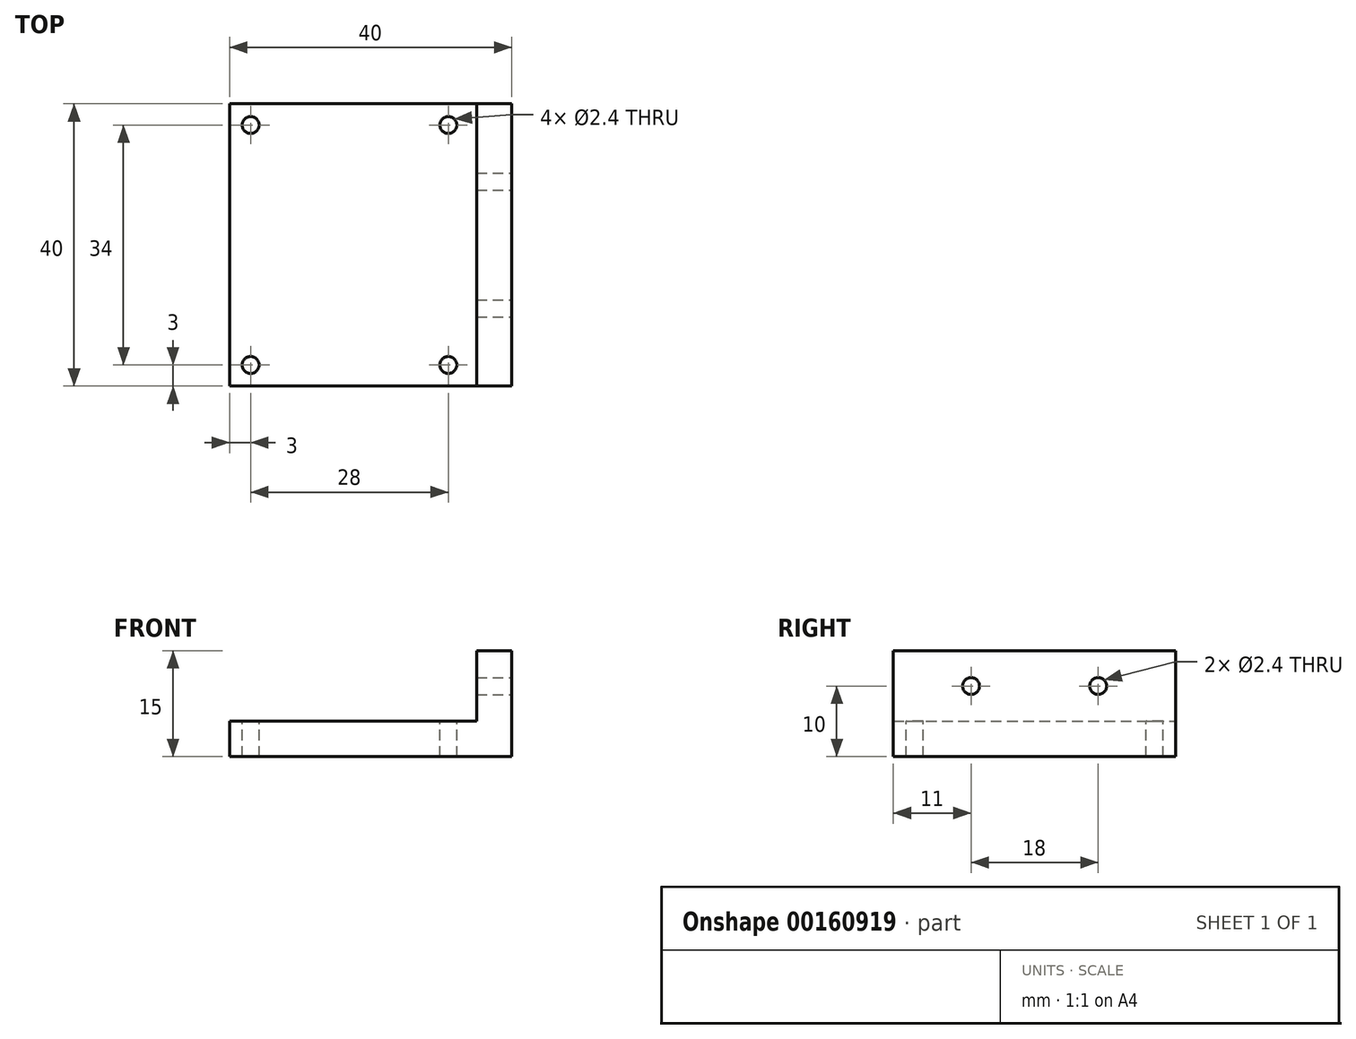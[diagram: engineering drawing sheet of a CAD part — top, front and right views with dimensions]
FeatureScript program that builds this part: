
annotation { "Feature Type Name" : "Feature", "Feature Type Description" : "" }
export const myFeature = defineFeature(function(context is Context, id is Id, definition is map)
    precondition{}
    {
        {
            var Q0;
            Q0=qCreatedBy(makeId("Top.planeOp"),FACE);
            var sketch = newSketch(context, id + "F0", { "sketchPlane" : qUnion([Q0])});
            skLineSegment(sketch, "E0.bottom", {"start": v(20, -20) * mm, "end": v(-20, -20) * mm});
            skLineSegment(sketch, "E0.top", {"start": v(20, 20) * mm, "end": v(-20, 20) * mm});
            skLineSegment(sketch, "E0.left", {"start": v(20, -20) * mm, "end": v(20, 20) * mm});
            skLineSegment(sketch, "E0.right", {"start": v(-20, -20) * mm, "end": v(-20, 20) * mm});
            skPoint(sketch, "E0.middle", {"position": v(0, 0) * mm});
            skSolve(sketch);
        }
        {
            var Q0;
            Q0 = qSketchRegion(id + "F0", true);
            extrude(context, id + "F1", {"entities" : qUnion([Q0]), "depth" : 5 * mm});
        }
        {
            var Q0;
            Q0=makeQuery(id+"F1.opExtrude","CAP_FACE",FACE,{"disambiguationData":[OSD([sQuery(id+"F0.wireOp",EDGE,"E0.bottom"),sQuery(id+"F0.wireOp",EDGE,"E0.top"),sQuery(id+"F0.wireOp",EDGE,"E0.left"),sQuery(id+"F0.wireOp",EDGE,"E0.right")])],"isStart":false});
            var sketch = newSketch(context, id + "F2", { "sketchPlane" : qUnion([Q0])});
            skLineSegment(sketch, "E1.bottom", {"start": v(20, 20) * mm, "end": v(15, 20) * mm});
            skLineSegment(sketch, "E1.top", {"start": v(20, -20) * mm, "end": v(15, -20) * mm});
            skLineSegment(sketch, "E1.left", {"start": v(20, 20) * mm, "end": v(20, -20) * mm});
            skLineSegment(sketch, "E1.right", {"start": v(15, 20) * mm, "end": v(15, -20) * mm});
            skSolve(sketch);
        }
        {
            var Q0;
            Q0 = qSketchRegion(id + "F2", true);
            extrude(context, id + "F3", {"entities" : qUnion([Q0]), "operationType" : NewBodyOperationType.ADD, "depth" : 10 * mm});
        }
        {
            var Q0;
            Q0=makeQuery(id+"F3.boolean.opBoolean","MERGE",FACE,{"derivedFrom":[makeQuery(id+"F1.opExtrude","SWEPT_FACE",FACE,{"disambiguationData":[OSD([sQuery(id+"F0.wireOp",EDGE,"E0.left")])]}),makeQuery(id+"F3.opExtrude","SWEPT_FACE",FACE,{"disambiguationData":[OSD([sQuery(id+"F2.wireOp",EDGE,"E1.left")])]})]});
            var sketch = newSketch(context, id + "F4", { "sketchPlane" : qUnion([Q0])});
            skPoint(sketch, "E2", {"position": v(-9, 10) * mm});
            skPoint(sketch, "E3", {"position": v(9, 10) * mm});
            skSolve(sketch);
        }
        {
            var Q0;
            Q0=sQuery(id+"F4.wireOp",VERTEX,"E2");
            var Q1;
            Q1=sQuery(id+"F4.wireOp",VERTEX,"E3");
            var Q2;
            Q2=makeQuery(id+"F1.opExtrude","SWEPT_BODY",BODY,{"disambiguationData":[OSD([sQuery(id+"F0.wireOp",EDGE,"E0.bottom"),sQuery(id+"F0.wireOp",EDGE,"E0.top"),sQuery(id+"F0.wireOp",EDGE,"E0.left"),sQuery(id+"F0.wireOp",EDGE,"E0.right")])]});
            hole(context, id + "F5", {"style" : HoleStyle.SIMPLE, "endStyle" : HoleEndStyle.THROUGH, "standardTappedOrClearance" : lookupTablePath({ "standard" : "ISO", "engagement" : "75%", "pitch" : "0.6 mm", "size" : "M3", "type" : "Tapped" }), "standardBlindInLast" : lookupTablePath({ "standard" : "ISO", "engagement" : "75%", "pitch" : "0.6 mm", "size" : "M3", "type" : "Tapped" }), "holeDiameter" : 2.4 * mm, "locations" : qUnion([Q0, Q1]), "scope" : qUnion([Q2]), "isTappedThrough" : true, "showTappedDepth" : true});
        }
        {
            var Q0;
            Q0=makeQuery(id+"F1.opExtrude","CAP_FACE",FACE,{"disambiguationData":[OSD([sQuery(id+"F0.wireOp",EDGE,"E0.bottom"),sQuery(id+"F0.wireOp",EDGE,"E0.top"),sQuery(id+"F0.wireOp",EDGE,"E0.left"),sQuery(id+"F0.wireOp",EDGE,"E0.right")])],"isStart":false});
            var sketch = newSketch(context, id + "F6", { "sketchPlane" : qUnion([Q0])});
            skPoint(sketch, "E4", {"position": v(-17, 17) * mm});
            skPoint(sketch, "E5", {"position": v(-17, -17) * mm});
            skPoint(sketch, "E6", {"position": v(11, -17) * mm});
            skPoint(sketch, "E7", {"position": v(11, 17) * mm});
            skSolve(sketch);
        }
        {
            var Q0;
            Q0=sQuery(id+"F6.wireOp",VERTEX,"E4");
            var Q1;
            Q1=sQuery(id+"F6.wireOp",VERTEX,"E7");
            var Q2;
            Q2=sQuery(id+"F6.wireOp",VERTEX,"E6");
            var Q3;
            Q3=sQuery(id+"F6.wireOp",VERTEX,"E5");
            var Q4;
            Q4=makeQuery(id+"F1.opExtrude","SWEPT_BODY",BODY,{"disambiguationData":[OSD([sQuery(id+"F0.wireOp",EDGE,"E0.bottom"),sQuery(id+"F0.wireOp",EDGE,"E0.top"),sQuery(id+"F0.wireOp",EDGE,"E0.left"),sQuery(id+"F0.wireOp",EDGE,"E0.right")])]});
            hole(context, id + "F7", {"style" : HoleStyle.SIMPLE, "endStyle" : HoleEndStyle.THROUGH, "standardTappedOrClearance" : lookupTablePath({ "standard" : "ISO", "engagement" : "75%", "pitch" : "0.6 mm", "size" : "M3", "type" : "Tapped" }), "standardBlindInLast" : lookupTablePath({ "standard" : "ISO", "engagement" : "75%", "pitch" : "0.6 mm", "size" : "M3", "type" : "Tapped" }), "holeDiameter" : 2.4 * mm, "locations" : qUnion([Q0, Q1, Q2, Q3]), "scope" : qUnion([Q4]), "isTappedThrough" : true, "showTappedDepth" : true});
        }
    });
